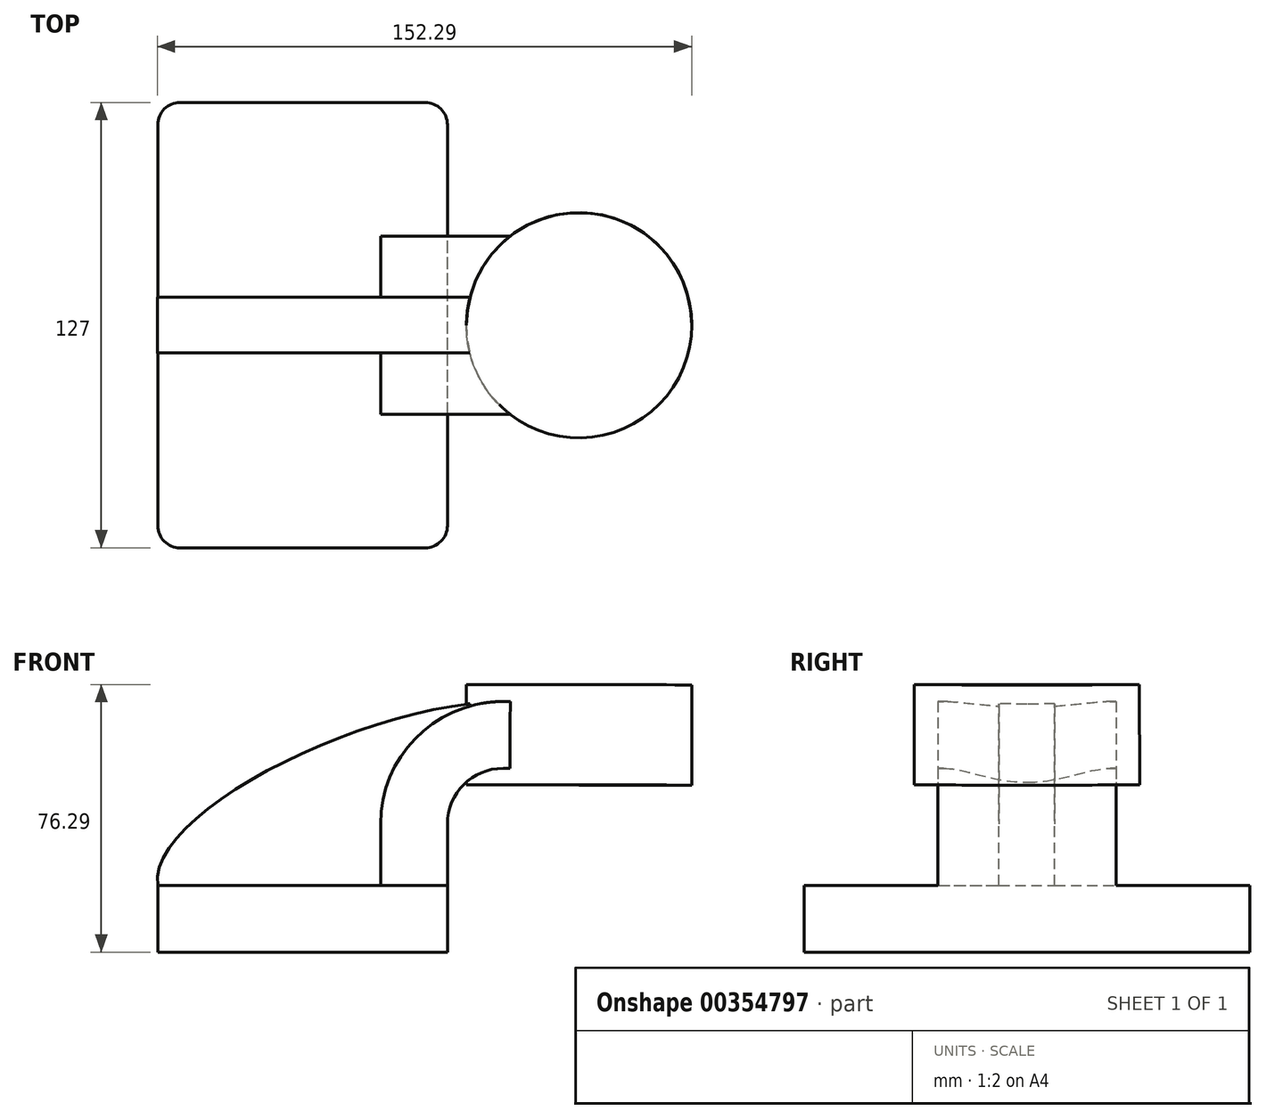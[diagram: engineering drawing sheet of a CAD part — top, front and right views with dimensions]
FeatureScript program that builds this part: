
annotation { "Feature Type Name" : "Feature", "Feature Type Description" : "" }
export const myFeature = defineFeature(function(context is Context, id is Id, definition is map)
    precondition{}
    {
        {
            var Q0;
            Q0=qCreatedBy(makeId("Front.planeOp"),FACE);
            var sketch = newSketch(context, id + "F0", { "sketchPlane" : qUnion([Q0])});
            skLineSegment(sketch, "E0.bottom", {"start": v(41.27, 9.53) * mm, "end": v(-41.28, 9.53) * mm});
            skLineSegment(sketch, "E0.top", {"start": v(41.28, -9.52) * mm, "end": v(-41.27, -9.52) * mm});
            skLineSegment(sketch, "E0.left", {"start": v(41.28, 9.53) * mm, "end": v(41.28, -9.52) * mm});
            skLineSegment(sketch, "E0.right", {"start": v(-41.28, 9.53) * mm, "end": v(-41.28, -9.52) * mm});
            skPoint(sketch, "E0.middle", {"position": v(0, 0) * mm});
            skLineSegment(sketch, "E1.bottom", {"start": v(110.9, 38.1) * mm, "end": v(60.1, 38.1) * mm});
            skLineSegment(sketch, "E1.top", {"start": v(110.9, 66.68) * mm, "end": v(60.1, 66.68) * mm});
            skLineSegment(sketch, "E1.left", {"start": v(110.9, 38.1) * mm, "end": v(110.9, 66.68) * mm});
            skLineSegment(sketch, "E1.right", {"start": v(60.1, 38.1) * mm, "end": v(60.1, 66.68) * mm});
            skLineSegment(sketch, "E2", {"start": v(41.27, 9.53) * mm, "end": v(41.27, 27) * mm});
            skArc(sketch, "E3", {"start": v(41.27, 27) * mm, "mid": v(45.92, 38.23) * mm, "end": v(57.15, 42.88) * mm});
            skLineSegment(sketch, "E4", {"start": v(57.15, 42.88) * mm, "end": v(78.8, 42.88) * mm});
            skLineSegment(sketch, "E5.0", {"start": v(57.15, 61.93) * mm, "end": v(78.8, 61.93) * mm});
            skArc(sketch, "E5.1", {"start": v(22.23, 27) * mm, "mid": v(32.45, 51.7) * mm, "end": v(57.15, 61.93) * mm});
            skLineSegment(sketch, "E5.2", {"start": v(22.22, 9.53) * mm, "end": v(22.22, 27) * mm});
            skLineSegment(sketch, "E6", {"start": v(78.77, 38.1) * mm, "end": v(78.8, 66.68) * mm});
            skFitSpline(sketch, "E7", {"points": [v(-41.28, 9.52) * mm, v(57.15, 61.93) * mm], "startDerivative": vector(-9.45, 62.14) * mm, "endDerivative": vector(116.57, 0.99) * mm});
            skSolve(sketch);
        }
        {
            var Q0;
            Q0=makeQuery(id+"F0.imprint","IMPRINT",FACE,{"disambiguationData":[TD([[makeQuery(id+"F0.imprint","IMPRINT",EDGE,{"derivedFrom":sQuery(id+"F0.wireOp",EDGE,"E0.top")}),-1.0]])]});
            extrude(context, id + "F1", {"entities" : qUnion([Q0]), "endBound" : BoundingType.SYMMETRIC, "depth" : 127 * mm});
        }
        {
            var Q0;
            {var subQ1=sQuery(id+"F0.wireOp",EDGE,"E2");Q0=makeQuery(id+"F0.imprint","IMPRINT",FACE,{"disambiguationData":[TD([[makeQuery(id+"F0.imprint","IMPRINT",EDGE,{"derivedFrom":subQ1}),1.0]])]});}
            var Q1;
            {var subQ0=sQuery(id+"F0.wireOp",EDGE,"E4");var subQ1=sQuery(id+"F0.wireOp",EDGE,"E1.right");var subQ2=makeQuery(id+"F0.imprint","INTERSECT",VERTEX,{"derivedFrom":[subQ1,subQ0]});Q1=makeQuery(id+"F0.imprint","IMPRINT",FACE,{"disambiguationData":[TD([[makeQuery(id+"F0.imprint","IMPRINT",EDGE,{"disambiguationData":[TD([[subQ2,-1.0]])],"derivedFrom":subQ1}),-1.0]])]});}
            extrude(context, id + "F2", {"entities" : qUnion([Q0, Q1]), "operationType" : NewBodyOperationType.ADD, "endBound" : BoundingType.SYMMETRIC, "depth" : 50.8 * mm});
        }
        {
            var Q0;
            {var subQ3=sQuery(id+"F0.wireOp",EDGE,"E5.2");Q0=makeQuery(id+"F0.imprint","IMPRINT",FACE,{"disambiguationData":[TD([[makeQuery(id+"F0.imprint","IMPRINT",EDGE,{"derivedFrom":subQ3}),1.0]])]});}
            extrude(context, id + "F3", {"entities" : qUnion([Q0]), "operationType" : NewBodyOperationType.ADD, "endBound" : BoundingType.SYMMETRIC, "depth" : 15.88 * mm});
        }
        {
            var Q0;
            {var subQ0=sQuery(id+"F0.wireOp",EDGE,"E1.left");Q0=makeQuery(id+"F0.imprint","IMPRINT",FACE,{"disambiguationData":[TD([[makeQuery(id+"F0.imprint","IMPRINT",EDGE,{"derivedFrom":subQ0}),1.0]])]});}
            var Q1;
            Q1=sQuery(id+"F0.wireOp",EDGE,"E6");
            revolve(context, id + "F4", {"operationType" : NewBodyOperationType.ADD, "entities" : qUnion([Q0]), "axis" : qUnion([Q1]), "revolveType" : RevolveType.FULL});
        }
        {
            var Q0;
            Q0=makeQuery(id+"F1.opExtrude","CAP_EDGE",EDGE,{"disambiguationData":[OSD([sQuery(id+"F0.wireOp",EDGE,"E0.left")])],"isStart":false});
            var Q1;
            Q1=makeQuery(id+"F1.opExtrude","CAP_EDGE",EDGE,{"disambiguationData":[OSD([sQuery(id+"F0.wireOp",EDGE,"E0.right")])],"isStart":false});
            var Q2;
            Q2=makeQuery(id+"F1.opExtrude","CAP_EDGE",EDGE,{"disambiguationData":[OSD([sQuery(id+"F0.wireOp",EDGE,"E0.left")])],"isStart":true});
            var Q3;
            Q3=makeQuery(id+"F1.opExtrude","CAP_EDGE",EDGE,{"disambiguationData":[OSD([sQuery(id+"F0.wireOp",EDGE,"E0.right")])],"isStart":true});
            fillet(context, id + "F5", {"entities" : qUnion([Q0, Q1, Q2, Q3]), "radius" : 6.35 * mm, "tangentPropagation" : true, "allowEdgeOverflow" : false});
        }
    });
